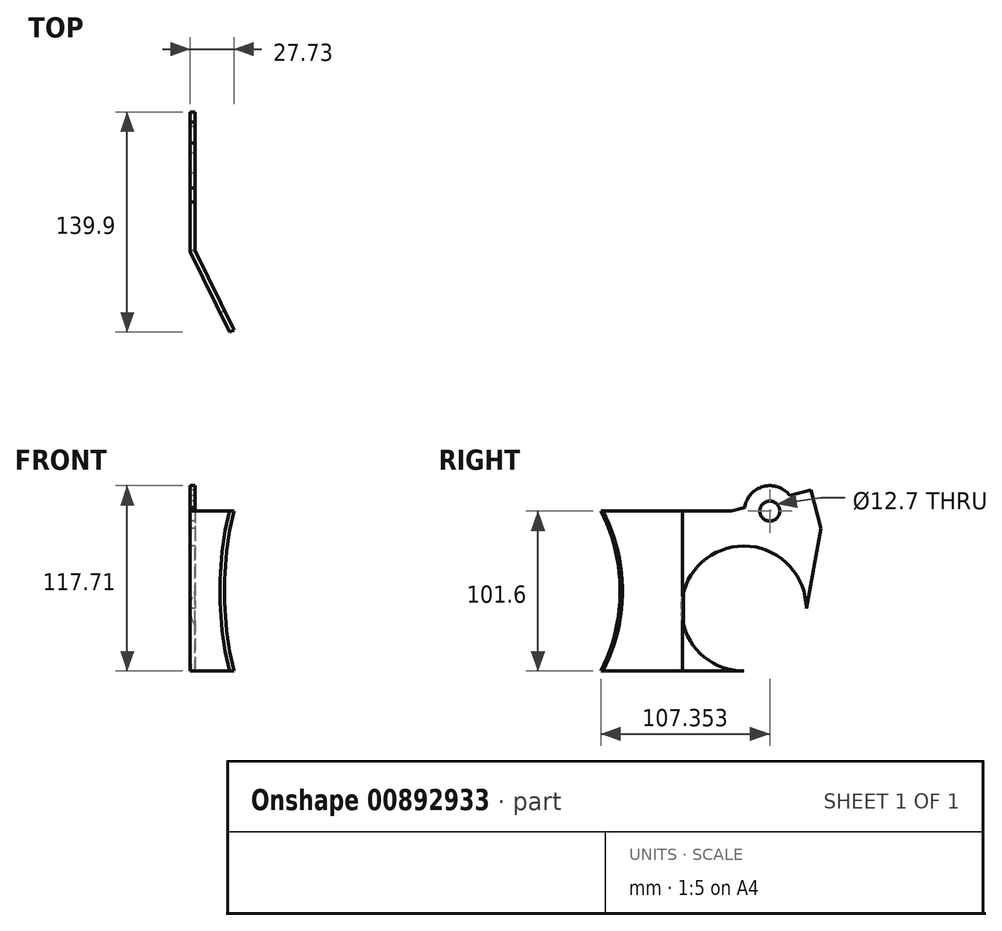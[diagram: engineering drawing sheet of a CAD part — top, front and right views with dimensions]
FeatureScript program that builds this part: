
annotation { "Feature Type Name" : "Feature", "Feature Type Description" : "" }
export const myFeature = defineFeature(function(context is Context, id is Id, definition is map)
    precondition{}
    {
        {
            var Q0;
            Q0=qCreatedBy(makeId("Top.planeOp"),FACE);
            var sketch = newSketch(context, id + "F0", { "sketchPlane" : qUnion([Q0])});
            skLineSegment(sketch, "E0", {"start": v(-209, -0.23) * mm, "end": v(-209, 39.45) * mm});
            skCircle(sketch, "E1", {"center": v(-165.93, -26.1) * mm, "radius": 22.23 * mm});
            skLineSegment(sketch, "E2", {"start": v(-184.13, -51.33) * mm, "end": v(349.8, -0.23) * mm});
            skLineSegment(sketch, "E3.0", {"start": v(349.8, 39.44) * mm, "end": v(-209, 39.44) * mm});
            skLineSegment(sketch, "E4", {"start": v(-209, -0.23) * mm, "end": v(-184.13, -51.33) * mm});
            skLineSegment(sketch, "E5", {"start": v(-209, -0.23) * mm, "end": v(349.8, -0.23) * mm});
            skLineSegment(sketch, "E6", {"start": v(349.8, 39.44) * mm, "end": v(349.8, -0.23) * mm});
            skSolve(sketch);
        }
        {
            var Q0;
            Q0=sQuery(id+"F0.wireOp",EDGE,"E4");
            cPlane(context, id + "F1", {"entities" : qUnion([Q0]), "cplaneType" : CPlaneType.LINE_ANGLE, "offset" : 25.4 * mm, "angle" : 90 * degree, "oppositeDirection" : true, "width" : 152.4 * mm, "height" : 152.4 * mm});
        }
        {
            var Q0;
            Q0=qCreatedBy(id+"F1.planeOp",FACE);
            var sketch = newSketch(context, id + "F2", { "sketchPlane" : qUnion([Q0])});
            skLineSegment(sketch, "E7.0", {"start": v(-91.27, 101.6) * mm, "end": v(-34.45, 101.6) * mm});
            skArc(sketch, "E8", {"start": v(-34.45, 101.6) * mm, "mid": v(-48.06, 50.8) * mm, "end": v(-34.45, 0) * mm});
            skLineSegment(sketch, "E9", {"start": v(-91.27, 101.6) * mm, "end": v(-91.27, 0) * mm});
            skLineSegment(sketch, "E10", {"start": v(-91.27, 0) * mm, "end": v(-34.45, 0) * mm});
            skSolve(sketch);
        }
        {
            var Q0;
            Q0=sQuery(id+"F0.wireOp",EDGE,"E0");
            cPlane(context, id + "F3", {"entities" : qUnion([Q0]), "cplaneType" : CPlaneType.LINE_ANGLE, "offset" : 25.4 * mm, "angle" : 90 * degree, "oppositeDirection" : true, "width" : 152.4 * mm, "height" : 152.4 * mm});
        }
        {
            var Q0;
            Q0=makeQuery(id+"F2.imprint","IMPRINT",FACE,{"disambiguationData":[TD([[makeQuery(id+"F2.imprint","IMPRINT",EDGE,{"derivedFrom":sQuery(id+"F2.wireOp",EDGE,"E7.0")}),-1.0]])]});
            extrude(context, id + "F4", {"entities" : qUnion([Q0]), "oppositeDirection" : true, "depth" : 3.17 * mm, "offsetDistance" : 25.4 * mm});
        }
        {
            var Q0;
            Q0=qCreatedBy(id+"F3.planeOp",FACE);
            var sketch = newSketch(context, id + "F5", { "sketchPlane" : qUnion([Q0])});
            skCircle(sketch, "E11", {"center": v(-39.45, 39.69) * mm, "radius": 39.69 * mm});
            skPoint(sketch, "E12.0", {"position": v(0.23, 101.6) * mm});
            skLineSegment(sketch, "E13", {"start": v(0.23, 101.6) * mm, "end": v(0.23, 39.69) * mm});
            skLineSegment(sketch, "E14.bottom", {"start": v(-62.7, 162.55) * mm, "end": v(-19.76, 151.05) * mm, "construction": true});
            skLineSegment(sketch, "E14.left", {"start": v(-62.7, 162.55) * mm, "end": v(-75.85, 113.49) * mm, "construction": true});
            skLineSegment(sketch, "E14.right", {"start": v(-19.76, 151.05) * mm, "end": v(-32.91, 101.98) * mm, "construction": true});
            skArc(sketch, "E15", {"start": v(-75.85, 113.49) * mm, "mid": v(-60.13, 86.27) * mm, "end": v(-32.91, 101.98) * mm, "construction": true});
            skCircle(sketch, "E16", {"center": v(-56.02, 101.6) * mm, "radius": 6.35 * mm});
            skCircle(sketch, "E17", {"center": v(-56.02, 101.6) * mm, "radius": 9.53 * mm, "construction": true});
            skLineSegment(sketch, "E18", {"start": v(-41.23, 156.8) * mm, "end": v(-32.03, 154.34) * mm});
            skLineSegment(sketch, "E19", {"start": v(-32.03, 154.34) * mm, "end": v(-5.73, 252.48) * mm, "construction": true});
            skLineSegment(sketch, "E20", {"start": v(-5.73, 252.48) * mm, "end": v(-24.14, 257.4) * mm});
            skLineSegment(sketch, "E21", {"start": v(-24.14, 257.4) * mm, "end": v(-50.43, 159.27) * mm, "construction": true});
            skPoint(sketch, "E22", {"position": v(-79.14, 39.69) * mm});
            skLineSegment(sketch, "E23.0", {"start": v(-75.85, 113.49) * mm, "end": v(-68.56, 111.53) * mm, "construction": true});
            skLineSegment(sketch, "E24", {"start": v(0.23, 101.6) * mm, "end": v(-33.02, 101.6) * mm});
            skLineSegment(sketch, "E25", {"start": v(-32.91, 101.98) * mm, "end": v(-40.2, 103.93) * mm});
            skLineSegment(sketch, "E26", {"start": v(-68.56, 111.53) * mm, "end": v(-82, 115.13) * mm, "construction": true});
            skLineSegment(sketch, "E27", {"start": v(-82, 115.13) * mm, "end": v(-88.57, 90.6) * mm});
            skArc(sketch, "E28", {"start": v(-40.07, 103.9) * mm, "mid": v(-51.85, 117.16) * mm, "end": v(-68.68, 111.57) * mm});
            skLineSegment(sketch, "E29", {"start": v(-82, 115.13) * mm, "end": v(-68.56, 111.53) * mm});
            skLineSegment(sketch, "E30.trimOffspring", {"start": v(-40.2, 103.93) * mm, "end": v(-31.49, 101.6) * mm});
            skPoint(sketch, "E31.trimOffspring.end.orphan", {"position": v(-79.14, 101.6) * mm});
            skPoint(sketch, "E32", {"position": v(-39.45, 0) * mm});
            skLineSegment(sketch, "E33", {"start": v(0, 0) * mm, "end": v(-39.45, 0) * mm});
            skLineSegment(sketch, "E34", {"start": v(0.23, 39.69) * mm, "end": v(0, 0) * mm});
            skLineSegment(sketch, "E35", {"start": v(-88.57, 90.6) * mm, "end": v(-79.14, 39.69) * mm});
            skSolve(sketch);
        }
        {
            var Q0;
            {var subQ2=sQuery(id+"F5.wireOp",EDGE,"E13");Q0=makeQuery(id+"F5.imprint","IMPRINT",FACE,{"disambiguationData":[TD([[makeQuery(id+"F5.imprint","IMPRINT",EDGE,{"derivedFrom":subQ2}),-1.0]])]});}
            var Q1;
            {var subQ0=sQuery(id+"F5.wireOp",EDGE,"E33");Q1=makeQuery(id+"F5.imprint","IMPRINT",FACE,{"disambiguationData":[TD([[makeQuery(id+"F5.imprint","IMPRINT",EDGE,{"derivedFrom":subQ0}),-1.0]])]});}
            extrude(context, id + "F6", {"entities" : qUnion([Q0, Q1]), "operationType" : NewBodyOperationType.ADD, "oppositeDirection" : true, "depth" : 3.17 * mm, "offsetDistance" : 25.4 * mm});
        }
        {
            var Q0;
            Q0=makeQuery(id+"F6.opExtrude","SWEPT_EDGE",EDGE,{"disambiguationData":[OSD([sQuery(id+"F5.wireOp",EDGE,"E11"),sQuery(id+"F5.wireOp",EDGE,"E35")])]});
            var Q1;
            Q1=makeQuery(id+"F6.opExtrude","CAP_EDGE",EDGE,{"disambiguationData":[OSD([sQuery(id+"F5.wireOp",EDGE,"E35")])],"isStart":true});
            cPlane(context, id + "F7", {"entities" : qUnion([Q0, Q1]), "cplaneType" : CPlaneType.LINE_ANGLE, "offset" : 25.4 * mm, "angle" : 0 * degree, "width" : 152.4 * mm, "height" : 152.4 * mm});
        }
        {
            var Q0;
            Q0=qCreatedBy(id+"F7.planeOp",FACE);
            var sketch = newSketch(context, id + "F8", { "sketchPlane" : qUnion([Q0])});
            skPoint(sketch, "E36.0", {"position": v(-209, 53.44) * mm});
            skPoint(sketch, "E37.0", {"position": v(-205.83, 105.21) * mm});
            skLineSegment(sketch, "E38", {"start": v(-205.83, 105.21) * mm, "end": v(-164.55, 105.21) * mm});
            skLineSegment(sketch, "E39", {"start": v(-164.55, 105.21) * mm, "end": v(-132.8, 53.44) * mm});
            skPoint(sketch, "E40.0", {"position": v(-205.83, 53.44) * mm});
            skLineSegment(sketch, "E41", {"start": v(-132.8, 53.44) * mm, "end": v(-205.83, 53.44) * mm});
            skLineSegment(sketch, "E42", {"start": v(-205.83, 53.44) * mm, "end": v(-205.83, 105.21) * mm});
            skSolve(sketch);
        }
        {
            var Q0;
            Q0=makeQuery(id+"F6.opExtrude","CAP_EDGE",EDGE,{"disambiguationData":[OSD([sQuery(id+"F5.wireOp",EDGE,"E27")])],"isStart":true});
            var Q1;
            Q1=makeQuery(id+"F6.opExtrude","SWEPT_EDGE",EDGE,{"disambiguationData":[OSD([sQuery(id+"F5.wireOp",EDGE,"E27"),sQuery(id+"F5.wireOp",EDGE,"E29")])]});
            cPlane(context, id + "F9", {"entities" : qUnion([Q0, Q1]), "cplaneType" : CPlaneType.LINE_ANGLE, "offset" : 25.4 * mm, "angle" : 0 * degree, "oppositeDirection" : true, "width" : 152.4 * mm, "height" : 152.4 * mm});
        }
    });
